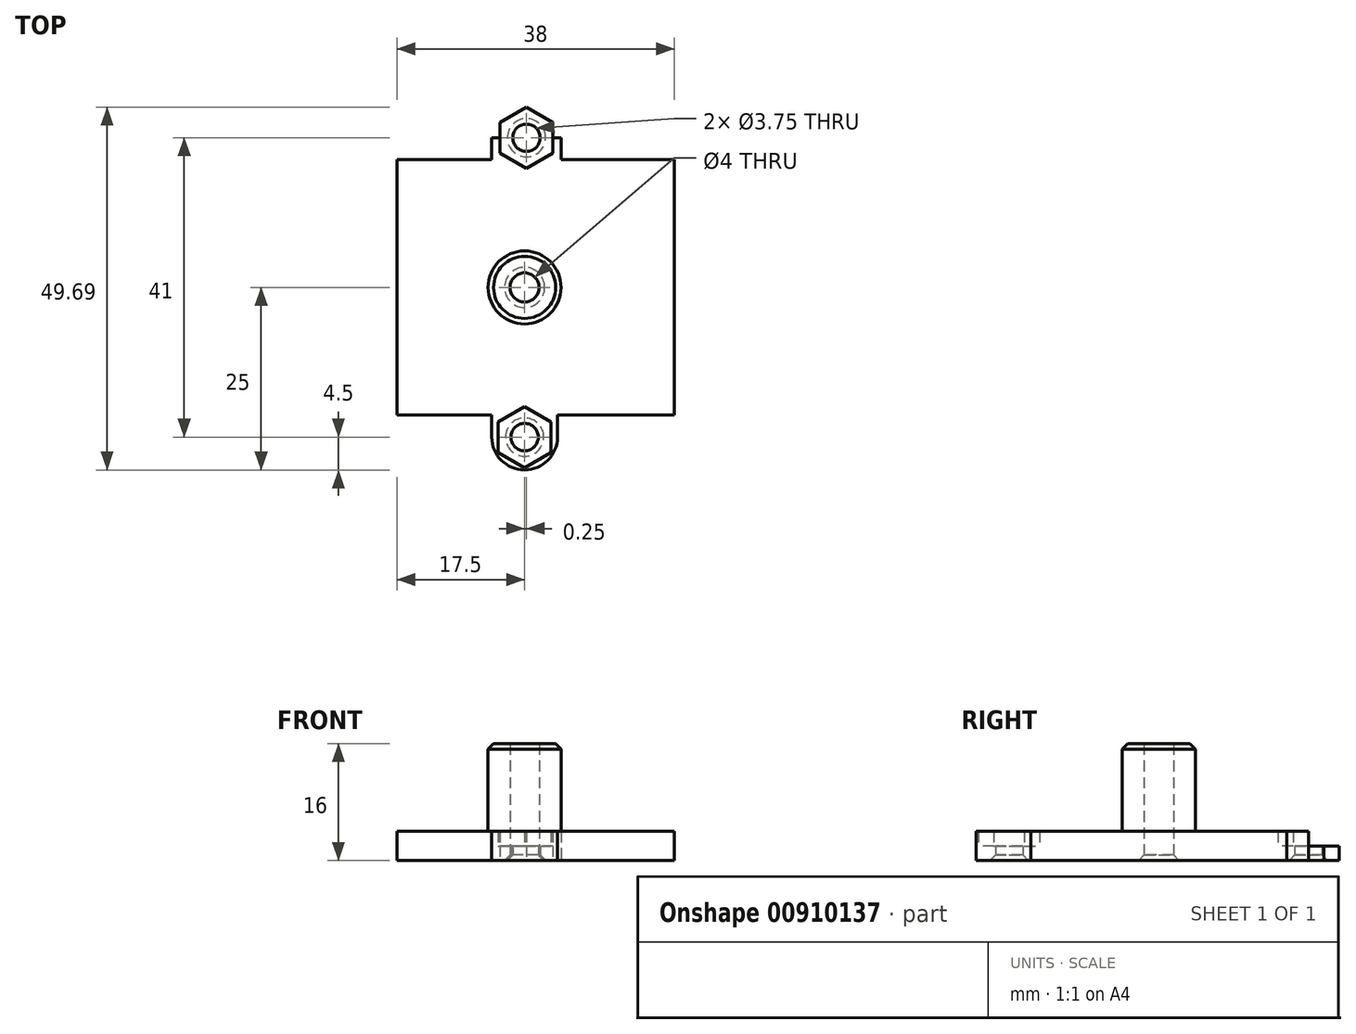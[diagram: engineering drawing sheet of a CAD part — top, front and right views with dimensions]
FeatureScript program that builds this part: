
annotation { "Feature Type Name" : "Feature", "Feature Type Description" : "" }
export const myFeature = defineFeature(function(context is Context, id is Id, definition is map)
    precondition{}
    {
        {
            var Q0;
            Q0=qCreatedBy(makeId("Top.planeOp"),FACE);
            var sketch = newSketch(context, id + "F0", { "sketchPlane" : qUnion([Q0])});
            skCircle(sketch, "E0", {"center": v(0, 0) * mm, "radius": 2 * mm});
            skCircle(sketch, "E1", {"center": v(0, 0) * mm, "radius": 5 * mm});
            skLineSegment(sketch, "E2.bottom", {"start": v(-17.5, 17.5) * mm, "end": v(20.5, 17.5) * mm});
            skLineSegment(sketch, "E2.top", {"start": v(-17.5, -17.5) * mm, "end": v(20.5, -17.5) * mm});
            skLineSegment(sketch, "E2.left", {"start": v(-17.5, 17.5) * mm, "end": v(-17.5, -17.5) * mm});
            skLineSegment(sketch, "E2.right", {"start": v(20.5, 17.5) * mm, "end": v(20.5, -17.5) * mm});
            skLineSegment(sketch, "E3.bottom", {"start": v(-4.5, 17.5) * mm, "end": v(5, 17.5) * mm});
            skLineSegment(sketch, "E3.top", {"start": v(-4.5, 20.5) * mm, "end": v(5, 20.5) * mm});
            skLineSegment(sketch, "E3.left", {"start": v(-4.5, 17.5) * mm, "end": v(-4.5, 20.5) * mm});
            skLineSegment(sketch, "E3.right", {"start": v(5, 17.5) * mm, "end": v(5, 20.5) * mm});
            skLineSegment(sketch, "E4.bottom", {"start": v(-4.5, -17.5) * mm, "end": v(4.5, -17.5) * mm});
            skLineSegment(sketch, "E4.top", {"start": v(-4.5, -20.5) * mm, "end": v(4.5, -20.5) * mm});
            skLineSegment(sketch, "E4.left", {"start": v(-4.5, -17.5) * mm, "end": v(-4.5, -20.5) * mm});
            skLineSegment(sketch, "E4.right", {"start": v(4.5, -17.5) * mm, "end": v(4.5, -20.5) * mm});
            skArc(sketch, "E5", {"start": v(-4.5, 20.5) * mm, "mid": v(0.25, 25.25) * mm, "end": v(5, 20.5) * mm});
            skArc(sketch, "E6", {"start": v(-4.5, -20.5) * mm, "mid": v(0, -25) * mm, "end": v(4.5, -20.5) * mm});
            skCircle(sketch, "E7", {"center": v(0, -20.5) * mm, "radius": 1.88 * mm});
            skCircle(sketch, "E8", {"center": v(0.25, 20.5) * mm, "radius": 1.88 * mm});
            skCircle(sketch, "E9.cCircle", {"center": v(0, -20.5) * mm, "radius": 3.62 * mm, "construction": true});
            skLineSegment(sketch, "E9.0", {"start": v(-3.62, -22.6) * mm, "end": v(-3.62, -18.4) * mm});
            skLineSegment(sketch, "E9.1", {"start": v(-3.62, -18.4) * mm, "end": v(0, -16.31) * mm});
            skLineSegment(sketch, "E9.2", {"start": v(0, -16.31) * mm, "end": v(3.63, -18.4) * mm});
            skLineSegment(sketch, "E9.3", {"start": v(3.63, -18.4) * mm, "end": v(3.63, -22.6) * mm});
            skLineSegment(sketch, "E9.4", {"start": v(3.62, -22.6) * mm, "end": v(0, -24.69) * mm});
            skLineSegment(sketch, "E9.5", {"start": v(0, -24.69) * mm, "end": v(-3.63, -22.6) * mm});
            skPoint(sketch, "E9.0.midPoint", {"position": v(-3.62, -20.5) * mm});
            skCircle(sketch, "E10.cCircle", {"center": v(0.25, 20.5) * mm, "radius": 3.62 * mm, "construction": true});
            skLineSegment(sketch, "E10.0", {"start": v(-3.38, 18.4) * mm, "end": v(-3.38, 22.6) * mm});
            skLineSegment(sketch, "E10.1", {"start": v(-3.38, 22.6) * mm, "end": v(0.25, 24.69) * mm});
            skLineSegment(sketch, "E10.2", {"start": v(0.25, 24.69) * mm, "end": v(3.87, 22.6) * mm});
            skLineSegment(sketch, "E10.3", {"start": v(3.87, 22.6) * mm, "end": v(3.87, 18.4) * mm});
            skLineSegment(sketch, "E10.4", {"start": v(3.87, 18.4) * mm, "end": v(0.25, 16.31) * mm});
            skLineSegment(sketch, "E10.5", {"start": v(0.25, 16.31) * mm, "end": v(-3.38, 18.4) * mm});
            skPoint(sketch, "E10.0.midPoint", {"position": v(-3.38, 20.5) * mm});
            skSolve(sketch);
        }
        {
            var Q0;
            {var subQ5=sQuery(id+"F0.wireOp",EDGE,"E3.left");Q0=makeQuery(id+"F0.imprint","IMPRINT",FACE,{"disambiguationData":[TD([[makeQuery(id+"F0.imprint","IMPRINT",EDGE,{"derivedFrom":subQ5}),-1.0]])]});}
            var Q1;
            {var subQ5=sQuery(id+"F0.wireOp",EDGE,"E3.right");Q1=makeQuery(id+"F0.imprint","IMPRINT",FACE,{"disambiguationData":[TD([[makeQuery(id+"F0.imprint","IMPRINT",EDGE,{"derivedFrom":subQ5}),1.0]])]});}
            var Q2;
            {var subQ4=sQuery(id+"F0.wireOp",EDGE,"E5");Q2=makeQuery(id+"F0.imprint","IMPRINT",FACE,{"disambiguationData":[TD([[makeQuery(id+"F0.imprint","IMPRINT",EDGE,{"derivedFrom":subQ4}),-1.0]])]});}
            var Q3;
            Q3=makeQuery(id+"F0.imprint","IMPRINT",FACE,{"disambiguationData":[TD([[makeQuery(id+"F0.imprint","IMPRINT",EDGE,{"derivedFrom":sQuery(id+"F0.wireOp",EDGE,"E1")}),-1.0]])]});
            var Q4;
            {var subQ0=sQuery(id+"F0.wireOp",EDGE,"E4.left");Q4=makeQuery(id+"F0.imprint","IMPRINT",FACE,{"disambiguationData":[TD([[makeQuery(id+"F0.imprint","IMPRINT",EDGE,{"derivedFrom":subQ0}),1.0]])]});}
            var Q5;
            {var subQ5=sQuery(id+"F0.wireOp",EDGE,"E4.right");Q5=makeQuery(id+"F0.imprint","IMPRINT",FACE,{"disambiguationData":[TD([[makeQuery(id+"F0.imprint","IMPRINT",EDGE,{"derivedFrom":subQ5}),-1.0]])]});}
            var Q6;
            {var subQ4=sQuery(id+"F0.wireOp",EDGE,"E6");Q6=makeQuery(id+"F0.imprint","IMPRINT",FACE,{"disambiguationData":[TD([[makeQuery(id+"F0.imprint","IMPRINT",EDGE,{"derivedFrom":subQ4}),1.0]])]});}
            extrude(context, id + "F1", {"entities" : qUnion([Q0, Q1, Q2, Q3, Q4, Q5, Q6]), "depth" : 4 * mm, "offsetDistance" : 25 * mm});
        }
        {
            var Q0;
            {var subQ3=sQuery(id+"F0.wireOp",EDGE,"E10.1");Q0=makeQuery(id+"F0.imprint","IMPRINT",FACE,{"disambiguationData":[TD([[makeQuery(id+"F0.imprint","IMPRINT",EDGE,{"derivedFrom":subQ3}),-1.0]])]});}
            var Q1;
            {var subQ8=sQuery(id+"F0.wireOp",EDGE,"E10.5");var subQ9=sQuery(id+"F0.wireOp",EDGE,"E2.bottom");var subQ10=makeQuery(id+"F0.imprint","INTERSECT",VERTEX,{"derivedFrom":[subQ9,subQ8]});Q1=makeQuery(id+"F0.imprint","IMPRINT",FACE,{"disambiguationData":[TD([[makeQuery(id+"F0.imprint","IMPRINT",EDGE,{"disambiguationData":[TD([[subQ10,-1.0]])],"derivedFrom":subQ9}),1.0]])]});}
            var Q2;
            {var subQ0=sQuery(id+"F0.wireOp",EDGE,"E10.5");var subQ1=sQuery(id+"F0.wireOp",EDGE,"E2.bottom");var subQ2=makeQuery(id+"F0.imprint","INTERSECT",VERTEX,{"derivedFrom":[subQ1,subQ0]});Q2=makeQuery(id+"F0.imprint","IMPRINT",FACE,{"disambiguationData":[TD([[makeQuery(id+"F0.imprint","IMPRINT",EDGE,{"disambiguationData":[TD([[subQ2,-1.0]])],"derivedFrom":subQ1}),-1.0]])]});}
            var Q3;
            {var subQ0=sQuery(id+"F0.wireOp",EDGE,"E9.1");var subQ1=sQuery(id+"F0.wireOp",EDGE,"E2.top");var subQ2=makeQuery(id+"F0.imprint","INTERSECT",VERTEX,{"derivedFrom":[subQ1,subQ0]});Q3=makeQuery(id+"F0.imprint","IMPRINT",FACE,{"disambiguationData":[TD([[makeQuery(id+"F0.imprint","IMPRINT",EDGE,{"disambiguationData":[TD([[subQ2,-1.0]])],"derivedFrom":subQ1}),1.0]])]});}
            var Q4;
            {var subQ10=sQuery(id+"F0.wireOp",EDGE,"E9.1");var subQ12=sQuery(id+"F0.wireOp",EDGE,"E2.top");var subQ13=makeQuery(id+"F0.imprint","INTERSECT",VERTEX,{"derivedFrom":[subQ12,subQ10]});Q4=makeQuery(id+"F0.imprint","IMPRINT",FACE,{"disambiguationData":[TD([[makeQuery(id+"F0.imprint","IMPRINT",EDGE,{"disambiguationData":[TD([[subQ13,-1.0]])],"derivedFrom":subQ12}),-1.0]])]});}
            var Q5;
            {var subQ7=sQuery(id+"F0.wireOp",EDGE,"E9.4");Q5=makeQuery(id+"F0.imprint","IMPRINT",FACE,{"disambiguationData":[TD([[makeQuery(id+"F0.imprint","IMPRINT",EDGE,{"derivedFrom":subQ7}),-1.0]])]});}
            extrude(context, id + "F2", {"entities" : qUnion([Q0, Q1, Q2, Q3, Q4, Q5]), "operationType" : NewBodyOperationType.ADD, "depth" : 2 * mm, "offsetDistance" : 25 * mm});
        }
        {
            var Q0;
            Q0=makeQuery(id+"F0.imprint","IMPRINT",FACE,{"disambiguationData":[TD([[makeQuery(id+"F0.imprint","IMPRINT",EDGE,{"derivedFrom":sQuery(id+"F0.wireOp",EDGE,"E0")}),-1.0]])]});
            extrude(context, id + "F3", {"entities" : qUnion([Q0]), "operationType" : NewBodyOperationType.ADD, "depth" : 16 * mm, "offsetDistance" : 25 * mm});
        }
        {
            var Q0;
            Q0=makeQuery(id+"F3.opExtrude","CAP_EDGE",EDGE,{"disambiguationData":[OSD([sQuery(id+"F0.wireOp",EDGE,"E1")])],"isStart":false});
            chamfer(context, id + "F4", {"entities" : qUnion([Q0]), "width" : 0.75 * mm, "tangentPropagation" : true});
        }
        {
            var Q0;
            Q0=makeQuery(id+"F2.opExtrude","CAP_EDGE",EDGE,{"disambiguationData":[OSD([sQuery(id+"F0.wireOp",EDGE,"E7")])],"isStart":true});
            var Q1;
            Q1=makeQuery(id+"F2.opExtrude","CAP_EDGE",EDGE,{"disambiguationData":[OSD([sQuery(id+"F0.wireOp",EDGE,"E8")])],"isStart":true});
            var Q2;
            Q2=makeQuery(id+"F3.opExtrude","CAP_EDGE",EDGE,{"disambiguationData":[OSD([sQuery(id+"F0.wireOp",EDGE,"E0")])],"isStart":true});
            chamfer(context, id + "F5", {"entities" : qUnion([Q0, Q1, Q2]), "width" : 0.75 * mm, "tangentPropagation" : true});
        }
    });
